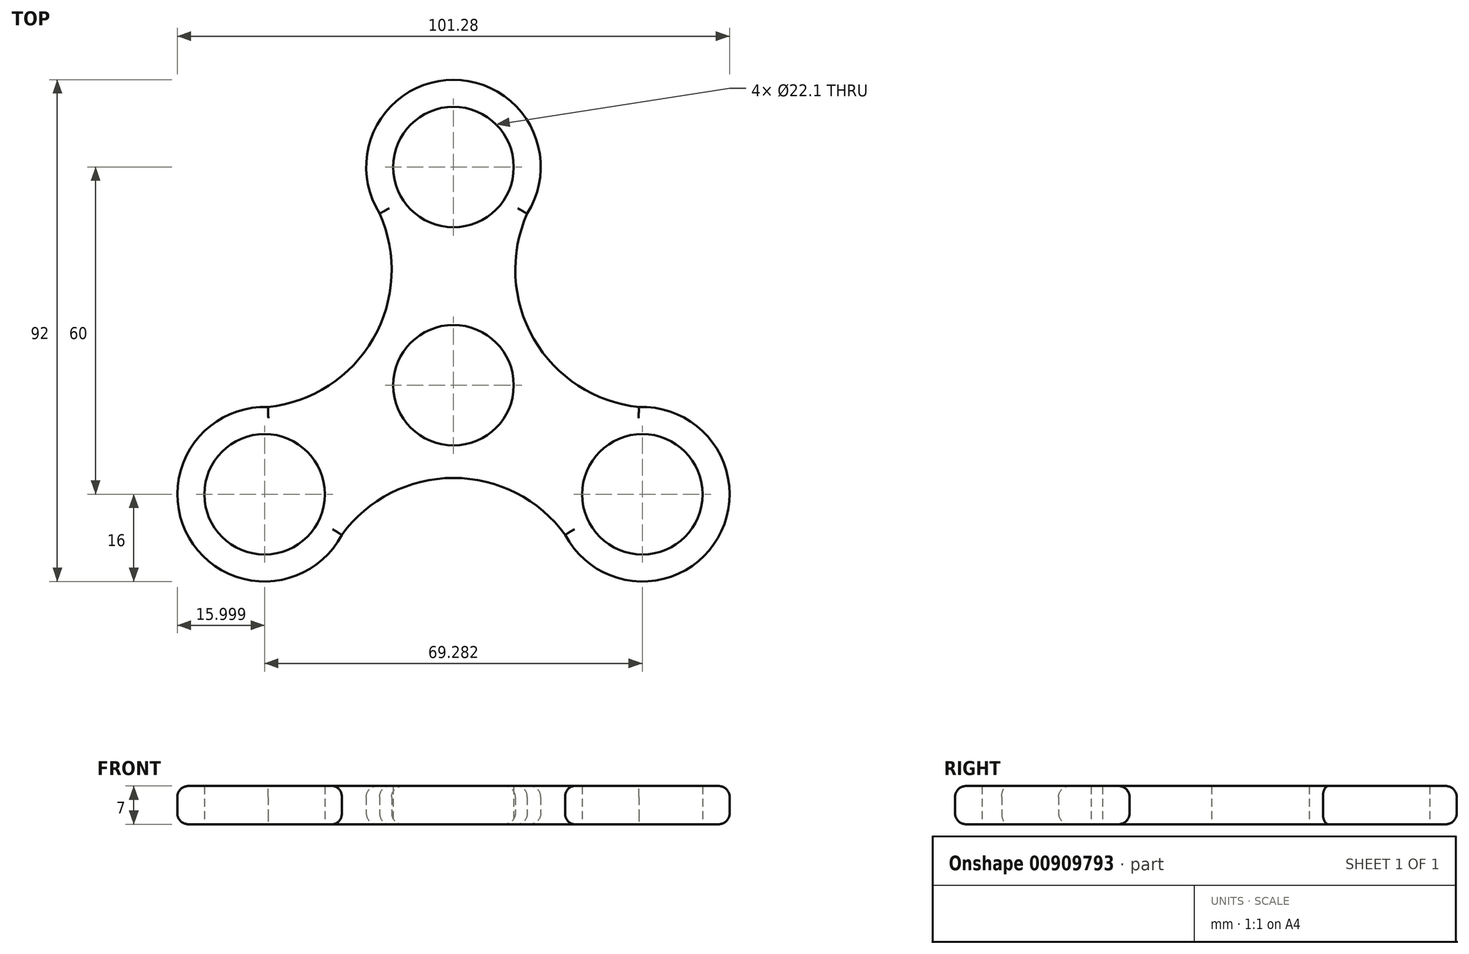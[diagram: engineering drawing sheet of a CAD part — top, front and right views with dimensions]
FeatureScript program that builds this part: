
annotation { "Feature Type Name" : "Feature", "Feature Type Description" : "" }
export const myFeature = defineFeature(function(context is Context, id is Id, definition is map)
    precondition{}
    {
        {
            var Q0;
            Q0=qCreatedBy(makeId("Top.planeOp"),FACE);
            var sketch = newSketch(context, id + "F0", { "sketchPlane" : qUnion([Q0])});
            skCircle(sketch, "E0", {"center": v(0, 0) * mm, "radius": 11.05 * mm});
            skCircle(sketch, "E1", {"center": v(0, 40) * mm, "radius": 11.05 * mm});
            skCircle(sketch, "E2.1.0", {"center": v(-34.64, -20) * mm, "radius": 11.05 * mm});
            skCircle(sketch, "E2.2.0", {"center": v(34.64, -20) * mm, "radius": 11.05 * mm});
            skCircle(sketch, "E3", {"center": v(0, 40) * mm, "radius": 16 * mm});
            skCircle(sketch, "E4.1.0", {"center": v(-34.64, -20) * mm, "radius": 16 * mm});
            skCircle(sketch, "E4.2.0", {"center": v(34.64, -20) * mm, "radius": 16 * mm});
            skLineSegment(sketch, "E5", {"start": v(0, 40) * mm, "end": v(34.64, -20) * mm, "construction": true});
            skLineSegment(sketch, "E6", {"start": v(9.3, 38.78) * mm, "end": v(39.4, -13.33) * mm, "construction": true});
            skArc(sketch, "E7", {"start": v(13.53, 31.46) * mm, "mid": v(14.73, 8.5) * mm, "end": v(34.02, -4.01) * mm});
            skArc(sketch, "E8.1.0", {"start": v(-34.02, -4.01) * mm, "mid": v(-14.73, 8.5) * mm, "end": v(-13.53, 31.46) * mm});
            skArc(sketch, "E8.2.0", {"start": v(20.48, -27.45) * mm, "mid": v(0, -17) * mm, "end": v(-20.48, -27.45) * mm});
            skSolve(sketch);
        }
        {
            var Q0;
            Q0=makeQuery(id+"F0.imprint","IMPRINT",FACE,{"disambiguationData":[TD([[makeQuery(id+"F0.imprint","IMPRINT",EDGE,{"derivedFrom":sQuery(id+"F0.wireOp",EDGE,"E2.1.0")}),-1.0]])]});
            var Q1;
            Q1=makeQuery(id+"F0.imprint","IMPRINT",FACE,{"disambiguationData":[TD([[makeQuery(id+"F0.imprint","IMPRINT",EDGE,{"derivedFrom":sQuery(id+"F0.wireOp",EDGE,"E0")}),-1.0]])]});
            var Q2;
            Q2=makeQuery(id+"F0.imprint","IMPRINT",FACE,{"disambiguationData":[TD([[makeQuery(id+"F0.imprint","IMPRINT",EDGE,{"derivedFrom":sQuery(id+"F0.wireOp",EDGE,"E1")}),-1.0]])]});
            var Q3;
            Q3=makeQuery(id+"F0.imprint","IMPRINT",FACE,{"disambiguationData":[TD([[makeQuery(id+"F0.imprint","IMPRINT",EDGE,{"derivedFrom":sQuery(id+"F0.wireOp",EDGE,"E2.2.0")}),-1.0]])]});
            extrude(context, id + "F1", {"entities" : qUnion([Q0, Q1, Q2, Q3]), "depth" : 7 * mm, "offsetDistance" : 25 * mm});
        }
        {
            var Q0;
            Q0=makeQuery(id+"F1.opExtrude","CAP_EDGE",EDGE,{"disambiguationData":[OSD([sQuery(id+"F0.wireOp",EDGE,"E3")])],"isStart":false});
            var Q1;
            Q1=makeQuery(id+"F1.opExtrude","CAP_EDGE",EDGE,{"disambiguationData":[OSD([sQuery(id+"F0.wireOp",EDGE,"E8.1.0")])],"isStart":false});
            var Q2;
            Q2=makeQuery(id+"F1.opExtrude","CAP_EDGE",EDGE,{"disambiguationData":[OSD([sQuery(id+"F0.wireOp",EDGE,"E4.1.0")])],"isStart":false});
            var Q3;
            Q3=makeQuery(id+"F1.opExtrude","CAP_EDGE",EDGE,{"disambiguationData":[OSD([sQuery(id+"F0.wireOp",EDGE,"E8.2.0")])],"isStart":false});
            var Q4;
            Q4=makeQuery(id+"F1.opExtrude","CAP_EDGE",EDGE,{"disambiguationData":[OSD([sQuery(id+"F0.wireOp",EDGE,"E7")])],"isStart":false});
            var Q5;
            Q5=makeQuery(id+"F1.opExtrude","CAP_EDGE",EDGE,{"disambiguationData":[OSD([sQuery(id+"F0.wireOp",EDGE,"E4.2.0")])],"isStart":false});
            var Q6;
            Q6=makeQuery(id+"F1.opExtrude","CAP_EDGE",EDGE,{"disambiguationData":[OSD([sQuery(id+"F0.wireOp",EDGE,"E8.1.0")])],"isStart":true});
            var Q7;
            Q7=makeQuery(id+"F1.opExtrude","CAP_EDGE",EDGE,{"disambiguationData":[OSD([sQuery(id+"F0.wireOp",EDGE,"E3")])],"isStart":true});
            var Q8;
            Q8=makeQuery(id+"F1.opExtrude","CAP_EDGE",EDGE,{"disambiguationData":[OSD([sQuery(id+"F0.wireOp",EDGE,"E4.1.0")])],"isStart":true});
            var Q9;
            Q9=makeQuery(id+"F1.opExtrude","CAP_EDGE",EDGE,{"disambiguationData":[OSD([sQuery(id+"F0.wireOp",EDGE,"E8.2.0")])],"isStart":true});
            var Q10;
            Q10=makeQuery(id+"F1.opExtrude","CAP_EDGE",EDGE,{"disambiguationData":[OSD([sQuery(id+"F0.wireOp",EDGE,"E7")])],"isStart":true});
            var Q11;
            Q11=makeQuery(id+"F1.opExtrude","CAP_EDGE",EDGE,{"disambiguationData":[OSD([sQuery(id+"F0.wireOp",EDGE,"E4.2.0")])],"isStart":true});
            fillet(context, id + "F2", {"entities" : qUnion([Q0, Q1, Q2, Q3, Q4, Q5, Q6, Q7, Q8, Q9, Q10, Q11]), "radius" : 2 * mm, "tangentPropagation" : true, "allowEdgeOverflow" : false});
        }
    });
